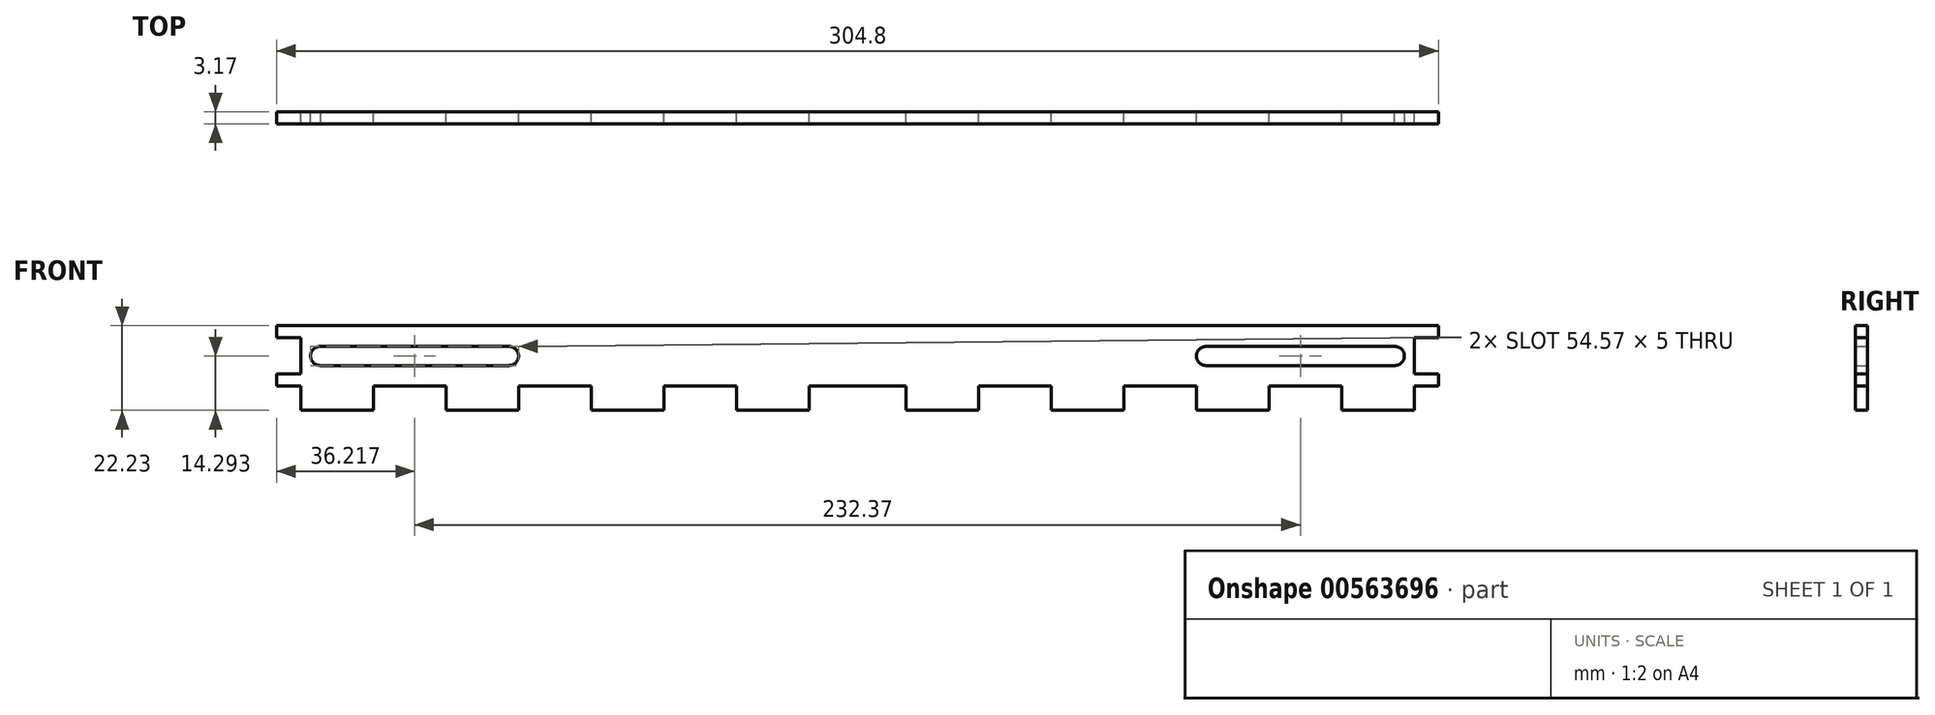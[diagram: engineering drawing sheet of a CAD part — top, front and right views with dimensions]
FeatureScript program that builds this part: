
annotation { "Feature Type Name" : "Feature", "Feature Type Description" : "" }
export const myFeature = defineFeature(function(context is Context, id is Id, definition is map)
    precondition{}
    {
        {
            var Q0;
            Q0=qCreatedBy(makeId("Front.planeOp"),FACE);
            var sketch = newSketch(context, id + "F0", { "sketchPlane" : qUnion([Q0])});
            skLineSegment(sketch, "E0", {"start": v(-178.04, 12.7) * mm, "end": v(114.06, 12.7) * mm});
            skLineSegment(sketch, "E1", {"start": v(-184.39, 12.7) * mm, "end": v(-178.04, 12.7) * mm});
            skLineSegment(sketch, "E2", {"start": v(-184.39, 12.7) * mm, "end": v(-184.39, 9.53) * mm});
            skLineSegment(sketch, "E3", {"start": v(-178.04, 9.53) * mm, "end": v(-184.39, 9.53) * mm});
            skLineSegment(sketch, "E4", {"start": v(-178.04, 9.53) * mm, "end": v(-178.04, 0) * mm});
            skLineSegment(sketch, "E5", {"start": v(-184.39, 0) * mm, "end": v(-178.04, 0) * mm});
            skLineSegment(sketch, "E6", {"start": v(-184.39, 0) * mm, "end": v(-184.39, -3.17) * mm});
            skLineSegment(sketch, "E7", {"start": v(-178.04, -3.17) * mm, "end": v(-184.39, -3.17) * mm});
            skLineSegment(sketch, "E8", {"start": v(-178.04, -3.17) * mm, "end": v(-178.04, -9.53) * mm});
            skLineSegment(sketch, "E9", {"start": v(-31.99, 12.7) * mm, "end": v(-31.99, -20.37) * mm, "construction": true});
            skLineSegment(sketch, "E10.MirrorCS", {"start": v(114.06, 12.7) * mm, "end": v(114.06, 12.7) * mm});
            skLineSegment(sketch, "E11.MirrorCS", {"start": v(120.41, 12.7) * mm, "end": v(120.41, 9.52) * mm});
            skLineSegment(sketch, "E12.MirrorCS", {"start": v(120.41, 12.7) * mm, "end": v(114.06, 12.7) * mm});
            skLineSegment(sketch, "E13.MirrorCS", {"start": v(114.06, 9.52) * mm, "end": v(120.41, 9.52) * mm});
            skLineSegment(sketch, "E14.MirrorCS", {"start": v(120.41, 0) * mm, "end": v(114.06, 0) * mm});
            skLineSegment(sketch, "E15.MirrorCS", {"start": v(114.06, 9.52) * mm, "end": v(114.06, 0) * mm});
            skLineSegment(sketch, "E16.MirrorCS", {"start": v(114.06, -3.18) * mm, "end": v(114.06, -9.53) * mm});
            skLineSegment(sketch, "E17.MirrorCS", {"start": v(120.41, 0) * mm, "end": v(120.41, -3.18) * mm});
            skLineSegment(sketch, "E18.MirrorCS", {"start": v(114.06, -3.18) * mm, "end": v(120.41, -3.18) * mm});
            skLineSegment(sketch, "E19", {"start": v(-178.04, -9.53) * mm, "end": v(-158.99, -9.53) * mm});
            skLineSegment(sketch, "E20", {"start": v(-158.99, -9.53) * mm, "end": v(-158.99, -3.17) * mm});
            skLineSegment(sketch, "E21", {"start": v(-158.99, -3.17) * mm, "end": v(-139.94, -3.17) * mm});
            skLineSegment(sketch, "E22", {"start": v(-31.99, 4.76) * mm, "end": v(-120.89, 4.76) * mm, "construction": true});
            skLineSegment(sketch, "E23", {"start": v(-123.39, 7.26) * mm, "end": v(-172.96, 7.26) * mm});
            skLineSegment(sketch, "E24.MirrorCS", {"start": v(59.41, 7.26) * mm, "end": v(59.41, 7.26) * mm});
            skLineSegment(sketch, "E25.1.0.0", {"start": v(-139.94, -9.53) * mm, "end": v(-120.89, -9.53) * mm});
            skLineSegment(sketch, "E25.1.0.1", {"start": v(-120.89, -9.53) * mm, "end": v(-120.89, -3.17) * mm});
            skLineSegment(sketch, "E25.1.0.2", {"start": v(-139.94, -3.17) * mm, "end": v(-139.94, -9.53) * mm});
            skLineSegment(sketch, "E25.1.0.3", {"start": v(-120.89, -3.17) * mm, "end": v(-101.84, -3.17) * mm});
            skLineSegment(sketch, "E25.2.0.0", {"start": v(-101.84, -9.53) * mm, "end": v(-82.79, -9.53) * mm});
            skLineSegment(sketch, "E25.2.0.1", {"start": v(-82.79, -9.53) * mm, "end": v(-82.79, -3.17) * mm});
            skLineSegment(sketch, "E25.2.0.2", {"start": v(-101.84, -3.17) * mm, "end": v(-101.84, -9.53) * mm});
            skLineSegment(sketch, "E25.2.0.3", {"start": v(-82.79, -3.17) * mm, "end": v(-63.74, -3.17) * mm});
            skLineSegment(sketch, "E25.3.0.0", {"start": v(-63.74, -9.53) * mm, "end": v(-44.69, -9.53) * mm});
            skLineSegment(sketch, "E25.3.0.1", {"start": v(-44.69, -9.53) * mm, "end": v(-44.69, -3.17) * mm});
            skLineSegment(sketch, "E25.3.0.2", {"start": v(-63.74, -3.17) * mm, "end": v(-63.74, -9.53) * mm});
            skLineSegment(sketch, "E25.direction1", {"start": v(-178.04, -9.53) * mm, "end": v(-139.94, -9.53) * mm, "construction": true});
            skLineSegment(sketch, "E26.MirrorCS", {"start": v(114.06, -9.53) * mm, "end": v(95.01, -9.53) * mm});
            skLineSegment(sketch, "E27.MirrorCS", {"start": v(-0.24, -9.53) * mm, "end": v(-19.29, -9.53) * mm});
            skLineSegment(sketch, "E28.MirrorCS", {"start": v(37.86, -3.18) * mm, "end": v(37.86, -9.53) * mm});
            skLineSegment(sketch, "E29.MirrorCS", {"start": v(-19.29, -9.53) * mm, "end": v(-19.29, -3.18) * mm});
            skLineSegment(sketch, "E30.MirrorCS", {"start": v(75.96, -3.18) * mm, "end": v(75.96, -9.53) * mm});
            skLineSegment(sketch, "E31.MirrorCS", {"start": v(18.81, -9.53) * mm, "end": v(18.81, -3.18) * mm});
            skLineSegment(sketch, "E32.MirrorCS", {"start": v(56.91, -9.53) * mm, "end": v(56.91, -3.18) * mm});
            skLineSegment(sketch, "E33.MirrorCS", {"start": v(114.06, -9.53) * mm, "end": v(75.96, -9.53) * mm, "construction": true});
            skLineSegment(sketch, "E34.MirrorCS", {"start": v(75.96, -9.53) * mm, "end": v(56.91, -9.53) * mm});
            skLineSegment(sketch, "E35.MirrorCS", {"start": v(95.01, -9.53) * mm, "end": v(95.01, -3.18) * mm});
            skLineSegment(sketch, "E36.MirrorCS", {"start": v(37.86, -9.53) * mm, "end": v(18.81, -9.53) * mm});
            skLineSegment(sketch, "E37.MirrorCS", {"start": v(-0.24, -3.18) * mm, "end": v(-0.24, -9.53) * mm});
            skLineSegment(sketch, "E38.MirrorCS", {"start": v(95.01, -3.18) * mm, "end": v(75.96, -3.18) * mm});
            skLineSegment(sketch, "E39.MirrorCS", {"start": v(56.91, -3.18) * mm, "end": v(37.86, -3.18) * mm});
            skLineSegment(sketch, "E40.MirrorCS", {"start": v(18.81, -3.18) * mm, "end": v(-0.24, -3.18) * mm});
            skLineSegment(sketch, "E41", {"start": v(-44.69, -3.17) * mm, "end": v(-19.29, -3.18) * mm});
            skArc(sketch, "E42", {"start": v(-123.39, 7.26) * mm, "mid": v(-120.89, 4.76) * mm, "end": v(-123.39, 2.26) * mm});
            skArc(sketch, "E43", {"start": v(-172.96, 7.26) * mm, "mid": v(-175.46, 4.71) * mm, "end": v(-172.86, 2.26) * mm});
            skLineSegment(sketch, "E44", {"start": v(-172.86, 2.26) * mm, "end": v(-123.39, 2.26) * mm});
            skLineSegment(sketch, "E45.MirrorCS", {"start": v(59.41, 7.26) * mm, "end": v(108.98, 7.26) * mm});
            skArc(sketch, "E46.MirrorCS", {"start": v(59.41, 7.26) * mm, "mid": v(56.91, 4.76) * mm, "end": v(59.41, 2.26) * mm});
            skLineSegment(sketch, "E47.MirrorCS", {"start": v(108.89, 2.26) * mm, "end": v(59.41, 2.26) * mm});
            skArc(sketch, "E48.MirrorCS", {"start": v(108.98, 7.26) * mm, "mid": v(111.48, 4.71) * mm, "end": v(108.89, 2.26) * mm});
            skSolve(sketch);
        }
        {
            var Q0;
            Q0=makeQuery(id+"F0.imprint","IMPRINT",FACE,{"disambiguationData":[TD([[makeQuery(id+"F0.imprint","IMPRINT",EDGE,{"derivedFrom":sQuery(id+"F0.wireOp",EDGE,"E0")}),-1.0]])]});
            extrude(context, id + "F1", {"entities" : qUnion([Q0]), "depth" : 3.17 * mm, "offsetDistance" : 25.4 * mm});
        }
    });
